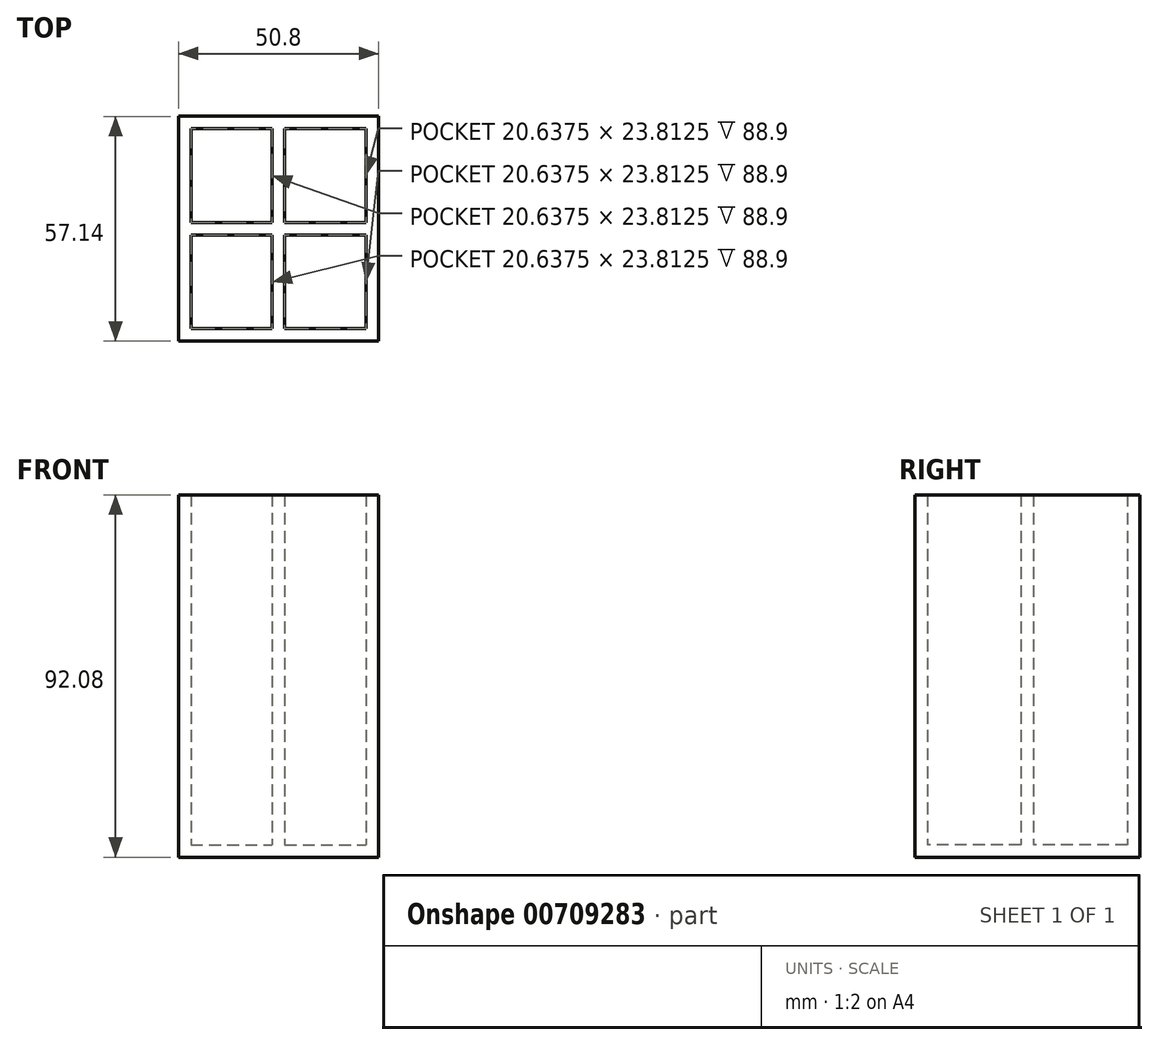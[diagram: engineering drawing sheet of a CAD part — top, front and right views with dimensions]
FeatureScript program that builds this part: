
annotation { "Feature Type Name" : "Feature", "Feature Type Description" : "" }
export const myFeature = defineFeature(function(context is Context, id is Id, definition is map)
    precondition{}
    {
        {
            var Q0;
            Q0=qCreatedBy(makeId("Top.planeOp"),FACE);
            var sketch = newSketch(context, id + "F0", { "sketchPlane" : qUnion([Q0])});
            skLineSegment(sketch, "E0.bottom", {"start": v(25.4, 28.58) * mm, "end": v(-25.4, 28.58) * mm});
            skLineSegment(sketch, "E0.top", {"start": v(25.4, -28.57) * mm, "end": v(-25.4, -28.57) * mm});
            skLineSegment(sketch, "E0.left", {"start": v(25.4, 28.58) * mm, "end": v(25.4, -28.57) * mm});
            skLineSegment(sketch, "E0.right", {"start": v(-25.4, 28.58) * mm, "end": v(-25.4, -28.57) * mm});
            skPoint(sketch, "E0.middle", {"position": v(0, 0) * mm});
            skSolve(sketch);
        }
        {
            var Q0;
            Q0=makeQuery(id+"F0.imprint","IMPRINT",FACE,{"disambiguationData":[TD([[makeQuery(id+"F0.imprint","IMPRINT",EDGE,{"derivedFrom":sQuery(id+"F0.wireOp",EDGE,"E0.bottom")}),1.0]])]});
            extrude(context, id + "F1", {"entities" : qUnion([Q0]), "depth" : 3.17 * mm, "offsetDistance" : 25.4 * mm});
        }
        {
            var Q0;
            Q0=makeQuery(id+"F1.opExtrude","CAP_FACE",FACE,{"disambiguationData":[OSD([sQuery(id+"F0.wireOp",EDGE,"E0.bottom"),sQuery(id+"F0.wireOp",EDGE,"E0.top"),sQuery(id+"F0.wireOp",EDGE,"E0.left"),sQuery(id+"F0.wireOp",EDGE,"E0.right")])],"isStart":false});
            var sketch = newSketch(context, id + "F2", { "sketchPlane" : qUnion([Q0])});
            skLineSegment(sketch, "E1.bottom", {"start": v(-25.4, 28.58) * mm, "end": v(25.4, 28.58) * mm});
            skLineSegment(sketch, "E1.top", {"start": v(-25.4, 25.4) * mm, "end": v(25.4, 25.4) * mm});
            skLineSegment(sketch, "E1.left", {"start": v(-25.4, 28.58) * mm, "end": v(-25.4, 25.4) * mm});
            skLineSegment(sketch, "E1.right", {"start": v(25.4, 28.58) * mm, "end": v(25.4, 25.4) * mm});
            skSolve(sketch);
        }
        {
            var Q0;
            Q0 = qSketchRegion(id + "F2", true);
            extrude(context, id + "F3", {"entities" : qUnion([Q0]), "operationType" : NewBodyOperationType.ADD, "depth" : 88.9 * mm, "offsetDistance" : 25.4 * mm});
        }
        {
            var Q0;
            Q0=makeQuery(id+"F1.opExtrude","CAP_FACE",FACE,{"disambiguationData":[OSD([sQuery(id+"F0.wireOp",EDGE,"E0.bottom"),sQuery(id+"F0.wireOp",EDGE,"E0.top"),sQuery(id+"F0.wireOp",EDGE,"E0.left"),sQuery(id+"F0.wireOp",EDGE,"E0.right")])],"isStart":false});
            var sketch = newSketch(context, id + "F4", { "sketchPlane" : qUnion([Q0])});
            skLineSegment(sketch, "E2.bottom", {"start": v(-25.4, -28.57) * mm, "end": v(25.4, -28.57) * mm});
            skLineSegment(sketch, "E2.top", {"start": v(-25.4, -25.4) * mm, "end": v(25.4, -25.4) * mm});
            skLineSegment(sketch, "E2.left", {"start": v(-25.4, -28.57) * mm, "end": v(-25.4, -25.4) * mm});
            skLineSegment(sketch, "E2.right", {"start": v(25.4, -28.57) * mm, "end": v(25.4, -25.4) * mm});
            skSolve(sketch);
        }
        {
            var Q0;
            Q0 = qSketchRegion(id + "F4", true);
            extrude(context, id + "F5", {"entities" : qUnion([Q0]), "operationType" : NewBodyOperationType.ADD, "depth" : 88.9 * mm, "offsetDistance" : 25.4 * mm});
        }
        {
            var Q0;
            Q0=makeQuery(id+"F5.boolean.opBoolean","MERGE",FACE,{"derivedFrom":[makeQuery(id+"F3.boolean.opBoolean","MERGE",FACE,{"derivedFrom":[makeQuery(id+"F1.opExtrude","SWEPT_FACE",FACE,{"disambiguationData":[OSD([sQuery(id+"F0.wireOp",EDGE,"E0.left")])]}),makeQuery(id+"F3.opExtrude","SWEPT_FACE",FACE,{"disambiguationData":[OSD([sQuery(id+"F2.wireOp",EDGE,"E1.right")])]})]}),makeQuery(id+"F5.opExtrude","SWEPT_FACE",FACE,{"disambiguationData":[OSD([sQuery(id+"F4.wireOp",EDGE,"E2.right")])]})]});
            var sketch = newSketch(context, id + "F6", { "sketchPlane" : qUnion([Q0])});
            skLineSegment(sketch, "E3.bottom", {"start": v(-28.58, 92.08) * mm, "end": v(28.58, 92.08) * mm});
            skLineSegment(sketch, "E3.top", {"start": v(-28.58, 0) * mm, "end": v(28.58, 0) * mm});
            skLineSegment(sketch, "E3.left", {"start": v(-28.58, 92.08) * mm, "end": v(-28.58, 0) * mm});
            skLineSegment(sketch, "E3.right", {"start": v(28.58, 92.08) * mm, "end": v(28.58, 0) * mm});
            skSolve(sketch);
        }
        {
            var Q0;
            {var subQ1=sQuery(id+"F0.wireOp",EDGE,"E0.left");Q0=makeQuery(id+"F6.imprint","IMPRINT",FACE,{"disambiguationData":[TD([[makeQuery(id+"F6.imprint","IMPRINT",EDGE,{"derivedFrom":makeQuery(id+"F1.opExtrude","CAP_EDGE",EDGE,{"disambiguationData":[OSD([subQ1])],"isStart":false})}),-1.0]])]});}
            extrude(context, id + "F7", {"entities" : qUnion([Q0]), "operationType" : NewBodyOperationType.ADD, "depth" : -3.17 * mm, "offsetDistance" : 25.4 * mm});
        }
        {
            var Q0;
            Q0=makeQuery(id+"F5.boolean.opBoolean","MERGE",FACE,{"derivedFrom":[makeQuery(id+"F3.boolean.opBoolean","MERGE",FACE,{"derivedFrom":[makeQuery(id+"F1.opExtrude","SWEPT_FACE",FACE,{"disambiguationData":[OSD([sQuery(id+"F0.wireOp",EDGE,"E0.right")])]}),makeQuery(id+"F3.opExtrude","SWEPT_FACE",FACE,{"disambiguationData":[OSD([sQuery(id+"F2.wireOp",EDGE,"E1.left")])]})]}),makeQuery(id+"F5.opExtrude","SWEPT_FACE",FACE,{"disambiguationData":[OSD([sQuery(id+"F4.wireOp",EDGE,"E2.left")])]})]});
            var sketch = newSketch(context, id + "F8", { "sketchPlane" : qUnion([Q0])});
            skLineSegment(sketch, "E4.bottom", {"start": v(-28.58, 92.08) * mm, "end": v(28.57, 92.08) * mm});
            skLineSegment(sketch, "E4.top", {"start": v(-28.58, 0) * mm, "end": v(28.57, 0) * mm});
            skLineSegment(sketch, "E4.left", {"start": v(-28.58, 92.08) * mm, "end": v(-28.58, 0) * mm});
            skLineSegment(sketch, "E4.right", {"start": v(28.57, 92.08) * mm, "end": v(28.57, 0) * mm});
            skSolve(sketch);
        }
        {
            var Q0;
            {var subQ1=sQuery(id+"F0.wireOp",EDGE,"E0.right");Q0=makeQuery(id+"F8.imprint","IMPRINT",FACE,{"disambiguationData":[TD([[makeQuery(id+"F8.imprint","IMPRINT",EDGE,{"derivedFrom":makeQuery(id+"F1.opExtrude","CAP_EDGE",EDGE,{"disambiguationData":[OSD([subQ1])],"isStart":false})}),1.0]])]});}
            extrude(context, id + "F9", {"entities" : qUnion([Q0]), "operationType" : NewBodyOperationType.ADD, "depth" : -3.17 * mm, "offsetDistance" : 25.4 * mm});
        }
        {
            var Q0;
            Q0=makeQuery(id+"F1.opExtrude","CAP_FACE",FACE,{"disambiguationData":[OSD([sQuery(id+"F0.wireOp",EDGE,"E0.bottom"),sQuery(id+"F0.wireOp",EDGE,"E0.top"),sQuery(id+"F0.wireOp",EDGE,"E0.left"),sQuery(id+"F0.wireOp",EDGE,"E0.right")])],"isStart":false});
            var sketch = newSketch(context, id + "F10", { "sketchPlane" : qUnion([Q0])});
            skLineSegment(sketch, "E5.bottom", {"start": v(1.59, 25.4) * mm, "end": v(-1.59, 25.4) * mm});
            skLineSegment(sketch, "E5.top", {"start": v(1.59, -25.4) * mm, "end": v(-1.59, -25.4) * mm});
            skLineSegment(sketch, "E5.left", {"start": v(1.59, 25.4) * mm, "end": v(1.59, -25.4) * mm});
            skLineSegment(sketch, "E5.right", {"start": v(-1.59, 25.4) * mm, "end": v(-1.59, -25.4) * mm});
            skPoint(sketch, "E5.middle", {"position": v(0, 0) * mm});
            skSolve(sketch);
        }
        {
            var Q0;
            {var subQ0=sQuery(id+"F10.wireOp",EDGE,"E5.right");Q0=makeQuery(id+"F10.imprint","IMPRINT",FACE,{"disambiguationData":[TD([[makeQuery(id+"F10.imprint","IMPRINT",EDGE,{"derivedFrom":subQ0}),-1.0]])]});}
            var sketch = newSketch(context, id + "F11", { "sketchPlane" : qUnion([Q0])});
            skLineSegment(sketch, "E6.bottom", {"start": v(-22.23, 1.59) * mm, "end": v(22.23, 1.59) * mm});
            skLineSegment(sketch, "E6.top", {"start": v(-22.23, -1.59) * mm, "end": v(22.23, -1.59) * mm});
            skLineSegment(sketch, "E6.left", {"start": v(-22.23, 1.59) * mm, "end": v(-22.23, -1.59) * mm});
            skLineSegment(sketch, "E6.right", {"start": v(22.23, 1.59) * mm, "end": v(22.23, -1.59) * mm});
            skPoint(sketch, "E6.middle", {"position": v(0, 0) * mm});
            skSolve(sketch);
        }
        {
            var Q0;
            Q0 = qSketchRegion(id + "F11", true);
            extrude(context, id + "F12", {"entities" : qUnion([Q0]), "operationType" : NewBodyOperationType.ADD, "depth" : 88.9 * mm, "offsetDistance" : 25.4 * mm});
        }
        {
            var Q0;
            Q0 = qSketchRegion(id + "F10", true);
            extrude(context, id + "F13", {"entities" : qUnion([Q0]), "operationType" : NewBodyOperationType.ADD, "depth" : 88.9 * mm, "offsetDistance" : 25.4 * mm});
        }
    });
